# Revit family: FEDGE2-PD1500NDFSW
name_source: partatom
category: Leuchten
units: mm (PartAtom-declared; Revit-internal decimal feet)

## family parameters
Basisbauteil = Fläche
Beim Laden mit Abzugskörper schneiden = Nein
Bemaßung runder Anschluss = Durchmesser verwenden
Gemeinsam genutzt = Nein
Lichtquelle = Ja
OmniClass-Nummer = 23.80.70.11
OmniClass-Titel = Luminaries for Internal Lighting
Raumberechnungspunkt = Nein
Teiletyp = Normal

## types (6) — shared parameters
Baugruppenkennzeichen = D5020200
Datei für fotometrisches Netz = FEDGE2-PD1500NDWS850-0400.IES
Emissionsform beim Rendern sichtbar = Nein
Farbfilter = 16777215
Farbtemperaturverschiebung bei Dämpfen der Lampe = <Keine Auswahl>
Hersteller = RIDI Leuchten GmbH
Lampe = LED
Neigungswinkel = 90.00°
URL = www.ridi.de
Von Breite des Rechtecks ausssenden = 1382 mm  [stored 4.53412 ft]
Von Länge des Rechtecks aussenden = 222 mm  [stored 0.728346 ft]
brand = RIDI
conformity mark = CE
electrical safety class = 1
height = 22 mm  [stored 0.0721785 ft]
ingress protection (IP) code = IP20
length = 1501 mm
nominal frequency = 50-60Hz
nominal voltage = 230
voltage type (AC, DC, UC) = AC
weight = 8,8
width = 341 mm
zero-valued in all types: Vorgabe-Ansicht

## per-type parameters (varying)
| type | Modell | Scheinlast | rated input power |
| FEDGE2-PD1500NDFSW830-0400 | 0627629AQ | 29 VA | 29 |
| FEDGE2-PD1500DAFSW830-0400 | 0637629AQ | 29 VA | 29 |
| FEDGE2-PD1500NDFSW840-0400 | 0627630AQ | 29 VA | 29 |
| FEDGE2-PD1500DAFSW840-0400 | 0637630AQ | 26 VA | 26 |
| FEDGE2-PD1500NDFSW850-0400 | 0627631AQ | 29 VA | 29 |
| FEDGE2-PD1500DAFSW850-0400 | 0637631AQ | 29 VA | 29 |

note: column(s) folded — value = type name in every type: product name

note: [stored X ft] marks values corroborated as IEEE doubles in the binary element streams (Revit-internal decimal feet)
